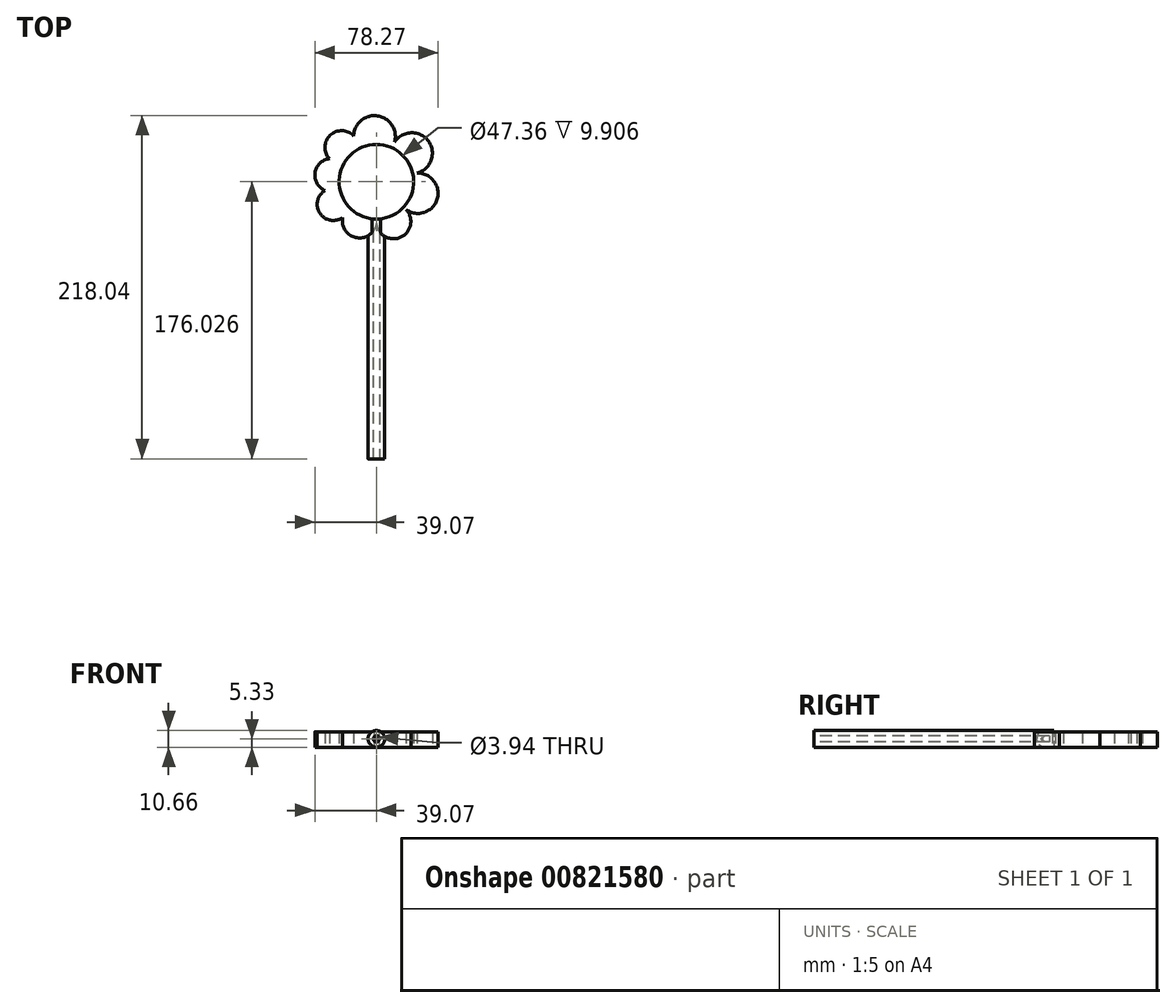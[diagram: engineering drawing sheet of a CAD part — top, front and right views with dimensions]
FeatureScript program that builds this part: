
annotation { "Feature Type Name" : "Feature", "Feature Type Description" : "" }
export const myFeature = defineFeature(function(context is Context, id is Id, definition is map)
    precondition{}
    {
        {
            var Q0;
            Q0=qCreatedBy(makeId("Front.planeOp"),FACE);
            var sketch = newSketch(context, id + "F0", { "sketchPlane" : qUnion([Q0])});
            skCircle(sketch, "E0", {"center": v(0, 0) * mm, "radius": 5.33 * mm});
            skSolve(sketch);
        }
        {
            var Q0;
            Q0=makeQuery(id+"F0.imprint","IMPRINT",FACE,{"disambiguationData":[TD([[makeQuery(id+"F0.imprint","IMPRINT",EDGE,{"derivedFrom":sQuery(id+"F0.wireOp",EDGE,"E0")}),1.0]])]});
            extrude(context, id + "F1", {"entities" : qUnion([Q0]), "depth" : 152.4 * mm, "offsetDistance" : 25.4 * mm});
        }
        {
            var Q0;
            Q0=makeQuery(id+"F1.opExtrude","CAP_FACE",FACE,{"disambiguationData":[OSD([sQuery(id+"F0.wireOp",EDGE,"E0")])],"isStart":false});
            var sketch = newSketch(context, id + "F2", { "sketchPlane" : qUnion([Q0])});
            skCircle(sketch, "E1", {"center": v(0, 0) * mm, "radius": 1.97 * mm});
            skSolve(sketch);
        }
        {
            var Q0;
            Q0 = qSketchRegion(id + "F2", true);
            extrude(context, id + "F3", {"entities" : qUnion([Q0]), "operationType" : NewBodyOperationType.REMOVE, "endBound" : BoundingType.THROUGH_ALL, "oppositeDirection" : true, "depth" : 25.4 * mm, "offsetDistance" : 25.4 * mm});
        }
        {
            var Q0;
            Q0=qCreatedBy(makeId("Top.planeOp"),FACE);
            var sketch = newSketch(context, id + "F4", { "sketchPlane" : qUnion([Q0])});
            skCircle(sketch, "E2", {"center": v(0, 23.63) * mm, "radius": 23.68 * mm});
            skArc(sketch, "E3", {"start": v(9.9, 45.14) * mm, "mid": v(-1.77, 65.63) * mm, "end": v(-11.67, 44.23) * mm});
            skArc(sketch, "E4", {"start": v(23.14, 28.66) * mm, "mid": v(32.67, 49.9) * mm, "end": v(9.9, 45.14) * mm});
            skArc(sketch, "E5", {"start": v(17.26, 7.42) * mm, "mid": v(38.74, 12.92) * mm, "end": v(23.14, 28.66) * mm});
            skArc(sketch, "E6", {"start": v(0, 0) * mm, "mid": v(15.24, -11.68) * mm, "end": v(17.26, 7.42) * mm});
            skArc(sketch, "E7", {"start": v(-17.26, 7.42) * mm, "mid": v(-15.02, -11.17) * mm, "end": v(0, 0) * mm});
            skArc(sketch, "E8", {"start": v(-23.16, 18.7) * mm, "mid": v(-36.45, 4.57) * mm, "end": v(-17.26, 7.42) * mm});
            skArc(sketch, "E9", {"start": v(-20.73, 35.06) * mm, "mid": v(-38.95, 29.4) * mm, "end": v(-23.16, 18.7) * mm});
            skArc(sketch, "E10", {"start": v(-11.67, 44.23) * mm, "mid": v(-29.65, 52.95) * mm, "end": v(-20.73, 35.06) * mm});
            skSolve(sketch);
        }
        {
            var Q0;
            Q0 = qSketchRegion(id + "F4", true);
            extrude(context, id + "F5", {"entities" : qUnion([Q0]), "operationType" : NewBodyOperationType.ADD, "depth" : 4.57 * mm, "offsetDistance" : 25.4 * mm, "hasSecondDirection" : true, "secondDirectionOppositeDirection" : true, "secondDirectionDepth" : 5.33 * mm});
        }
    });
